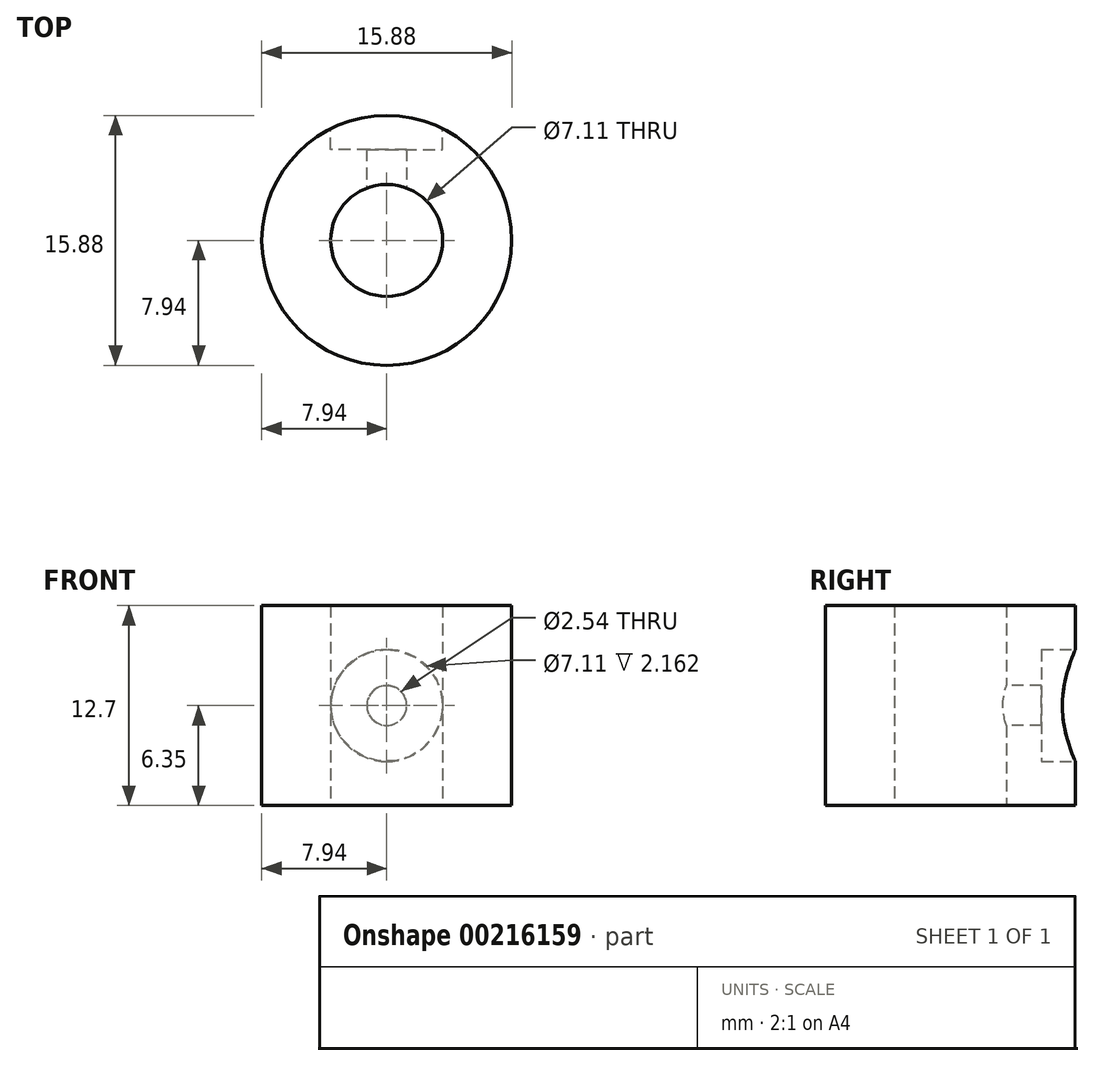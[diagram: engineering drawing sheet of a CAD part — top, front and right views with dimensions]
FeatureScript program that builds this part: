
annotation { "Feature Type Name" : "Feature", "Feature Type Description" : "" }
export const myFeature = defineFeature(function(context is Context, id is Id, definition is map)
    precondition{}
    {
        {
            var Q0;
            Q0=qCreatedBy(makeId("Top.planeOp"),FACE);
            var sketch = newSketch(context, id + "F0", { "sketchPlane" : qUnion([Q0])});
            skCircle(sketch, "E0", {"center": v(0, 0) * mm, "radius": 7.94 * mm});
            skCircle(sketch, "E1", {"center": v(0, 0) * mm, "radius": 3.56 * mm});
            skSolve(sketch);
        }
        {
            var Q0;
            Q0 = qSketchRegion(id + "F0", true);
            extrude(context, id + "F1", {"entities" : qUnion([Q0]), "depth" : 12.7 * mm});
        }
        {
            var Q0;
            Q0=qCreatedBy(makeId("Front.planeOp"),FACE);
            var sketch = newSketch(context, id + "F2", { "sketchPlane" : qUnion([Q0])});
            skCircle(sketch, "E2", {"center": v(0, 6.35) * mm, "radius": 1.27 * mm});
            skLineSegment(sketch, "E3", {"start": v(0, 0) * mm, "end": v(0, 6.35) * mm, "construction": true});
            skLineSegment(sketch, "E4", {"start": v(0, 6.35) * mm, "end": v(0, 12.7) * mm, "construction": true});
            skSolve(sketch);
        }
        {
            var Q0;
            Q0 = qSketchRegion(id + "F2", true);
            extrude(context, id + "F3", {"entities" : qUnion([Q0]), "operationType" : NewBodyOperationType.REMOVE, "endBound" : BoundingType.THROUGH_ALL, "oppositeDirection" : true, "depth" : 25.4 * mm});
        }
        {
            var Q0;
            Q0=qCreatedBy(makeId("Front.planeOp"),FACE);
            cPlane(context, id + "F4", {"entities" : qUnion([Q0]), "cplaneType" : CPlaneType.OFFSET, "offset" : 11.1 * mm, "oppositeDirection" : true, "width" : 152.4 * mm, "height" : 152.4 * mm});
        }
        {
            var Q0;
            Q0=qCreatedBy(id+"F4.planeOp",FACE);
            var sketch = newSketch(context, id + "F5", { "sketchPlane" : qUnion([Q0])});
            skCircle(sketch, "E5", {"center": v(0, 6.35) * mm, "radius": 3.56 * mm});
            skSolve(sketch);
        }
        {
            var Q0;
            Q0 = qSketchRegion(id + "F5", true);
            extrude(context, id + "F6", {"entities" : qUnion([Q0]), "operationType" : NewBodyOperationType.REMOVE, "depth" : 5.33 * mm});
        }
    });
